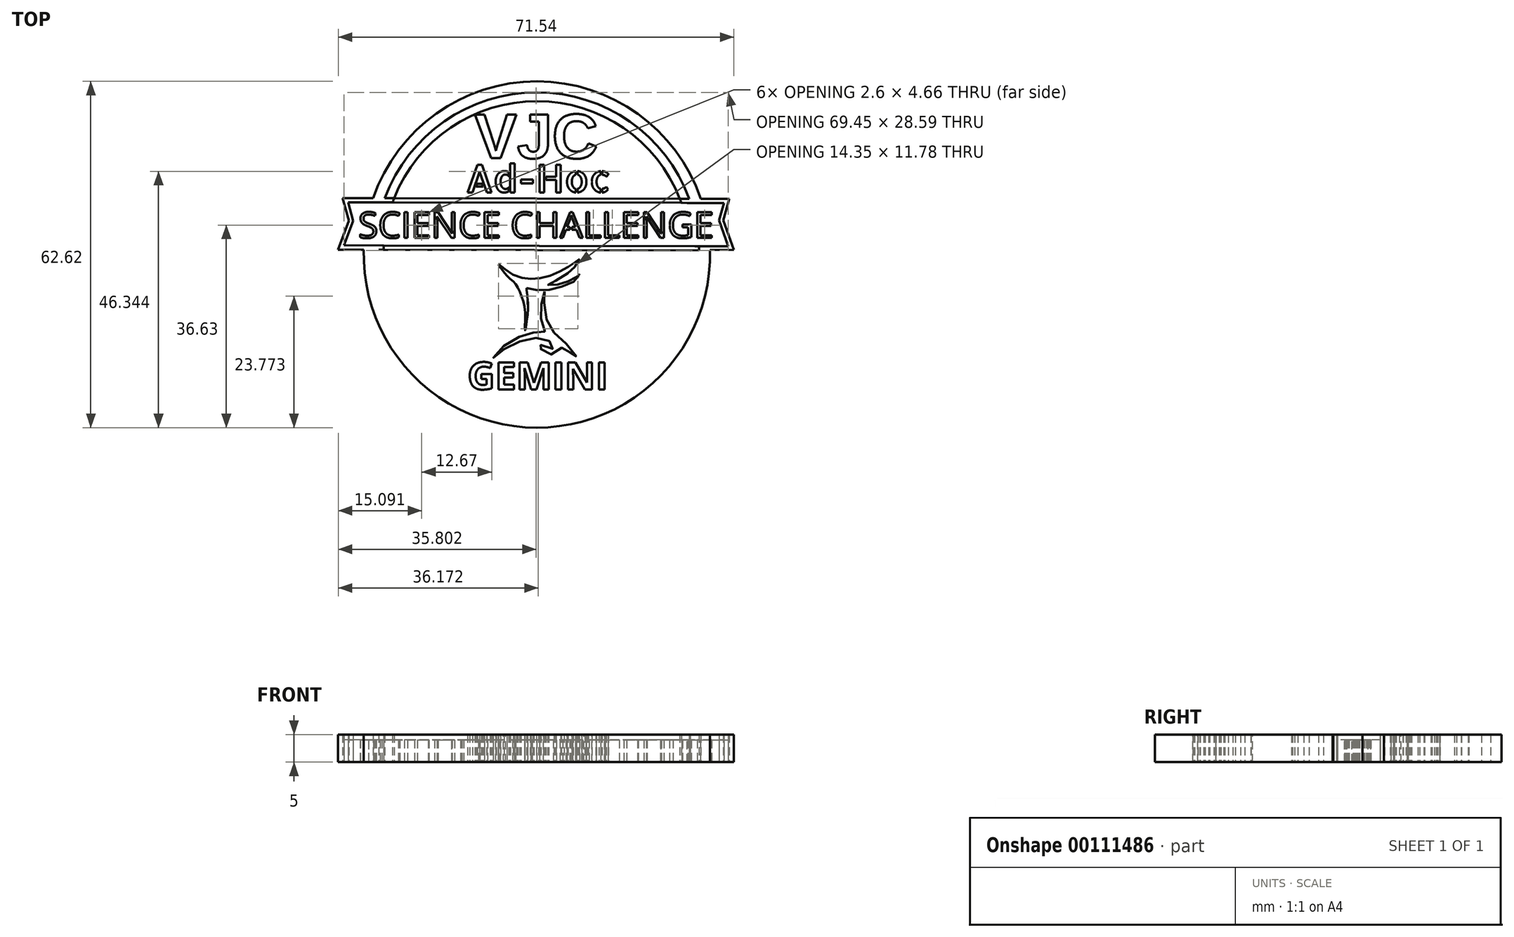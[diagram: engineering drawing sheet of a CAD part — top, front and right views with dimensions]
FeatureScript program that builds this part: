
annotation { "Feature Type Name" : "Feature", "Feature Type Description" : "" }
export const myFeature = defineFeature(function(context is Context, id is Id, definition is map)
    precondition{}
    {
        {
            var Q0;
            Q0=qCreatedBy(makeId("Top.planeOp"),FACE);
            var sketch = newSketch(context, id + "F0", { "sketchPlane" : qUnion([Q0])});
            skCircle(sketch, "E0", {"center": v(0.94, -3) * mm, "radius": 27.74 * mm});
            skPoint(sketch, "E0.first.point", {"position": v(1.58, 24.74) * mm});
            skPoint(sketch, "E0.second.point", {"position": v(0.52, -30.73) * mm});
            skPoint(sketch, "E0.third.point", {"position": v(-26.76, -1.33) * mm});
            skLineSegment(sketch, "E1", {"start": v(-24.87, 7.2) * mm, "end": v(-34.2, 7.2) * mm});
            skLineSegment(sketch, "E2", {"start": v(-34.2, 7.2) * mm, "end": v(-33.08, 3.11) * mm});
            skLineSegment(sketch, "E3", {"start": v(-33.08, 3.11) * mm, "end": v(-35, -2.1) * mm});
            skLineSegment(sketch, "E4", {"start": v(-35, -2.1) * mm, "end": v(-26.8, -2.1) * mm});
            skLineSegment(sketch, "E5", {"start": v(26.78, 7.1) * mm, "end": v(35.71, 7.1) * mm});
            skLineSegment(sketch, "E6", {"start": v(35.71, 7.1) * mm, "end": v(34.66, 3.21) * mm});
            skLineSegment(sketch, "E7", {"start": v(34.66, 3.21) * mm, "end": v(36.55, -2.1) * mm});
            skLineSegment(sketch, "E8", {"start": v(36.55, -2.1) * mm, "end": v(28.67, -2.25) * mm});
            skFitSpline(sketch, "E9", {"points": [v(-6, -4.72) * mm, v(-5.23, -5.35) * mm, v(-3.9, -6.35) * mm, v(-2.48, -6.98) * mm, v(-0.85, -7.35) * mm, v(0.35, -7.37) * mm, v(2.08, -7.15) * mm, v(3.86, -6.6) * mm, v(5.5, -5.84) * mm, v(6.83, -5.05) * mm, v(7.95, -4.34) * mm, v(8.2, -4.17) * mm, v(8.54, -3.89) * mm, v(8.14, -4.78) * mm, v(7.2, -5.82) * mm, v(5.2, -7.28) * mm, v(2.9, -8.45) * mm, v(3.98, -8.47) * mm, v(5.87, -8.12) * mm, v(7.76, -7.26) * mm, v(8.43, -6.75) * mm, v(8.6, -6.46) * mm, v(8.47, -7.15) * mm, v(6.46, -8.4) * mm, v(3.8, -9.28) * mm, v(1.11, -9.42) * mm, v(-0.95, -9.06) * mm], "startDerivative": vector(22.31, -18.25) * mm, "endDerivative": vector(-43, 9.84) * mm});
            skFitSpline(sketch, "E10", {"points": [v(-6, -4.72) * mm, v(-5.19, -6.01) * mm, v(-3.81, -7.48) * mm, v(-3.02, -8.2) * mm, v(-2.26, -9.47) * mm, v(-1.53, -11.45) * mm, v(-1.17, -13.95) * mm, v(-1.2, -16.67) * mm, v(-0.95, -15.45) * mm, v(-0.68, -11.98) * mm, v(-0.91, -9.36) * mm, v(-0.95, -9.06) * mm], "startDerivative": vector(8.3, -15) * mm, "endDerivative": vector(-0.86, 6) * mm});
            skFitSpline(sketch, "E11", {"points": [v(2.34, -9.66) * mm, v(2.02, -10.62) * mm, v(1.67, -12.76) * mm, v(1.67, -14.3) * mm, v(2.06, -16.19) * mm, v(2.36, -16.95) * mm, v(1.82, -16.92) * mm, v(-0.01, -17.17) * mm, v(-1.66, -17.64) * mm, v(-3.97, -18.79) * mm, v(-6.02, -20.44) * mm, v(-6.96, -21.68) * mm, v(-5.91, -20.77) * mm, v(-3.67, -19.33) * mm, v(-1.3, -18.4) * mm, v(0.83, -18.07) * mm, v(2.42, -18.3) * mm, v(3.7, -19.03) * mm, v(4.04, -19.68) * mm, v(3.45, -20.21) * mm, v(1.98, -19.81) * mm, v(1.3, -18.87) * mm, v(1.45, -19.8) * mm, v(2.36, -20.56) * mm, v(3.3, -21.02) * mm, v(4.84, -20.7) * mm, v(5.53, -19.8) * mm, v(6.38, -20.28) * mm, v(7.16, -20.84) * mm, v(8.14, -21.87) * mm, v(7.64, -20.68) * mm, v(6.28, -19.14) * mm, v(4.5, -17.53) * mm, v(3.33, -16.29) * mm, v(2.56, -14.18) * mm, v(2.24, -11.68) * mm, v(2.33, -10.24) * mm, v(2.34, -9.66) * mm]});
            skLineSegment(sketch, "E12", {"start": v(-24.87, 7.2) * mm, "end": v(28.1, 7.1) * mm});
            skLineSegment(sketch, "E13", {"start": v(-27.68, -2.1) * mm, "end": v(29.48, -2.24) * mm});
            skCircle(sketch, "E14.0", {"center": v(0.94, -3) * mm, "radius": 29.33 * mm});
            skCircle(sketch, "E15.0", {"center": v(0.94, -3) * mm, "radius": 31.31 * mm});
            skLineSegment(sketch, "E16.0", {"start": v(-24.87, 6.45) * mm, "end": v(28.1, 6.35) * mm});
            skLineSegment(sketch, "E17.0", {"start": v(-24.87, 6.45) * mm, "end": v(-33.21, 6.45) * mm});
            skLineSegment(sketch, "E18", {"start": v(28.1, 6.35) * mm, "end": v(34.73, 6.35) * mm});
            skLineSegment(sketch, "E19.0", {"start": v(-27.68, -1.35) * mm, "end": v(29.48, -1.49) * mm});
            skLineSegment(sketch, "E20", {"start": v(-27.68, -1.35) * mm, "end": v(-33.91, -1.33) * mm});
            skLineSegment(sketch, "E21", {"start": v(29.48, -1.49) * mm, "end": v(35.54, -1.5) * mm});
            skLineSegment(sketch, "E22.0", {"start": v(34.73, 6.35) * mm, "end": v(33.88, 3.18) * mm});
            skLineSegment(sketch, "E23.0", {"start": v(33.88, 3.18) * mm, "end": v(35.54, -1.5) * mm});
            skLineSegment(sketch, "E24.0", {"start": v(-32.3, 3.08) * mm, "end": v(-33.91, -1.33) * mm});
            skLineSegment(sketch, "E25.trimOffspring", {"start": v(-33.21, 6.45) * mm, "end": v(-32.3, 3.08) * mm});
            skText(sketch, "E26", { "text": "SCIENCE CHALLENGE", "fontName": "OpenSans-Regular.ttf"});
            skText(sketch, "E27", { "text": "GEMINI", "fontName": "OpenSans-Bold.ttf"});
            skText(sketch, "E28", { "text": "VJC", "fontName": "Arimo-Bold.ttf"});
            skLineSegment(sketch, "E29", {"start": v(6.9, 1.33) * mm, "end": v(6.9, 2.22) * mm});
            skLineSegment(sketch, "E30", {"start": v(6.9, 2.22) * mm, "end": v(7.18, 2.22) * mm});
            skLineSegment(sketch, "E31", {"start": v(7.18, 2.22) * mm, "end": v(7.26, 2.22) * mm});
            skLineSegment(sketch, "E32", {"start": v(7.26, 2.22) * mm, "end": v(7.26, 1.34) * mm});
            skLineSegment(sketch, "E33", {"start": v(7.26, 1.34) * mm, "end": v(6.9, 1.33) * mm});
            skText(sketch, "E34", { "text": "Ad-Hoc", "fontName": "AllertaStencil-Regular.ttf"});
            const initialGuessF0  = {"E26": [-0.03136, 0, 1, 0, 0.0047], "E27": [-0.0116, -0.02738, 1, 0, 0.00494], "E28": [-0.01032, 0.01442, 1, 0, 0.00826], "E34": [-0.012, 0.00825, 1, 0, 0.005]};
            skSetInitialGuess(sketch, initialGuessF0);
            skSolve(sketch);
        }
        {
            var Q0;
            Q0=makeQuery(id+"F0.imprint","IMPRINT",FACE,{"disambiguationData":[TD([[makeQuery(id+"F0.imprint","IMPRINT",EDGE,{"derivedFrom":sQuery(id+"F0.wireOp",EDGE,"f2c7ee9f-897c-4c1d-89b3-a48ac7c6bfa7.sketch_text.stroke-0")}),1.0]])]});
            var Q1;
            {var subQ0=sQuery(id+"F0.wireOp",EDGE,"E15.0");var subQ1=sQuery(id+"F0.wireOp",EDGE,"E1");var subQ2=makeQuery(id+"F0.imprint","INTERSECT",VERTEX,{"derivedFrom":[subQ1,subQ0]});Q1=makeQuery(id+"F0.imprint","IMPRINT",FACE,{"disambiguationData":[TD([[makeQuery(id+"F0.imprint","IMPRINT",EDGE,{"disambiguationData":[TD([[subQ2,1.0]])],"derivedFrom":subQ1}),-1.0]])]});}
            var Q2;
            Q2=makeQuery(id+"F0.imprint","IMPRINT",FACE,{"disambiguationData":[TD([[makeQuery(id+"F0.imprint","IMPRINT",EDGE,{"derivedFrom":sQuery(id+"F0.wireOp",EDGE,"26462852-2f77-49b2-9a3d-6dfd93b606f1.sketch_text.stroke-0")}),1.0]])]});
            var Q3;
            {var subQ0=sQuery(id+"F0.wireOp",EDGE,"E15.0");var subQ1=sQuery(id+"F0.wireOp",EDGE,"E4");var subQ2=makeQuery(id+"F0.imprint","INTERSECT",VERTEX,{"derivedFrom":[subQ1,subQ0]});Q3=makeQuery(id+"F0.imprint","IMPRINT",FACE,{"disambiguationData":[TD([[makeQuery(id+"F0.imprint","IMPRINT",EDGE,{"disambiguationData":[TD([[subQ2,-1.0]])],"derivedFrom":subQ1}),-1.0]])]});}
            var Q4;
            {var subQ7=sQuery(id+"F0.wireOp",EDGE,"E2");Q4=makeQuery(id+"F0.imprint","IMPRINT",FACE,{"disambiguationData":[TD([[makeQuery(id+"F0.imprint","IMPRINT",EDGE,{"derivedFrom":subQ7}),1.0]])]});}
            var Q5;
            {var subQ3=sQuery(id+"F0.wireOp",EDGE,"E17.0");var subQ10=makeQuery(id+"F0.imprint","IMPRINT",VERTEX,{"derivedFrom":subQ3});Q5=makeQuery(id+"F0.imprint","IMPRINT",FACE,{"disambiguationData":[TD([[makeQuery(id+"F0.imprint","IMPRINT",EDGE,{"disambiguationData":[TD([[subQ10,1.0]])],"derivedFrom":subQ3}),-1.0]])]});}
            var Q6;
            {var subQ0=sQuery(id+"F0.wireOp",EDGE,"E1");var subQ5=sQuery(id+"F0.wireOp",EDGE,"E14.0");var subQ6=makeQuery(id+"F0.imprint","INTERSECT",VERTEX,{"derivedFrom":[subQ0,subQ5]});Q6=makeQuery(id+"F0.imprint","IMPRINT",FACE,{"disambiguationData":[TD([[makeQuery(id+"F0.imprint","IMPRINT",EDGE,{"disambiguationData":[TD([[subQ6,-1.0]])],"derivedFrom":subQ5}),1.0]])]});}
            var Q7;
            {var subQ1=sQuery(id+"F0.wireOp",EDGE,"E5");var subQ6=sQuery(id+"F0.wireOp",EDGE,"E0");var subQ7=makeQuery(id+"F0.imprint","INTERSECT",VERTEX,{"derivedFrom":[subQ6,subQ1]});Q7=makeQuery(id+"F0.imprint","IMPRINT",FACE,{"disambiguationData":[TD([[makeQuery(id+"F0.imprint","IMPRINT",EDGE,{"disambiguationData":[TD([[subQ7,1.0]])],"derivedFrom":subQ6}),-1.0]])]});}
            var Q8;
            {var subQ0=sQuery(id+"F0.wireOp",EDGE,"E15.0");var subQ1=sQuery(id+"F0.wireOp",EDGE,"E5");var subQ2=makeQuery(id+"F0.imprint","INTERSECT",VERTEX,{"derivedFrom":[subQ1,subQ0]});Q8=makeQuery(id+"F0.imprint","IMPRINT",FACE,{"disambiguationData":[TD([[makeQuery(id+"F0.imprint","IMPRINT",EDGE,{"disambiguationData":[TD([[subQ2,1.0]])],"derivedFrom":subQ1}),-1.0]])]});}
            var Q9;
            {var subQ11=sQuery(id+"F0.wireOp",EDGE,"E6");Q9=makeQuery(id+"F0.imprint","IMPRINT",FACE,{"disambiguationData":[TD([[makeQuery(id+"F0.imprint","IMPRINT",EDGE,{"derivedFrom":subQ11}),-1.0]])]});}
            var Q10;
            {var subQ0=sQuery(id+"F0.wireOp",EDGE,"E13");var subQ1=sQuery(id+"F0.wireOp",EDGE,"E0");var subQ2=makeQuery(id+"F0.imprint","INTERSECT",VERTEX,{"disambiguationData":[OD(0.0)],"derivedFrom":[subQ1,subQ0]});Q10=makeQuery(id+"F0.imprint","IMPRINT",FACE,{"disambiguationData":[TD([[makeQuery(id+"F0.imprint","IMPRINT",EDGE,{"disambiguationData":[TD([[subQ2,-1.0]])],"derivedFrom":subQ1}),1.0]])]});}
            var Q11;
            {var subQ0=sQuery(id+"F0.wireOp",EDGE,"E13");var subQ3=sQuery(id+"F0.wireOp",EDGE,"E0");var subQ4=makeQuery(id+"F0.imprint","INTERSECT",VERTEX,{"disambiguationData":[OD(0.0)],"derivedFrom":[subQ3,subQ0]});Q11=makeQuery(id+"F0.imprint","IMPRINT",FACE,{"disambiguationData":[TD([[makeQuery(id+"F0.imprint","IMPRINT",EDGE,{"disambiguationData":[TD([[subQ4,-1.0]])],"derivedFrom":subQ3}),-1.0]])]});}
            var Q12;
            {var subQ0=sQuery(id+"F0.wireOp",EDGE,"E15.0");var subQ1=sQuery(id+"F0.wireOp",EDGE,"E8");var subQ2=makeQuery(id+"F0.imprint","INTERSECT",VERTEX,{"derivedFrom":[subQ1,subQ0]});Q12=makeQuery(id+"F0.imprint","IMPRINT",FACE,{"disambiguationData":[TD([[makeQuery(id+"F0.imprint","IMPRINT",EDGE,{"disambiguationData":[TD([[subQ2,-1.0]])],"derivedFrom":subQ1}),-1.0]])]});}
            var Q13;
            {var subQ0=sQuery(id+"F0.wireOp",EDGE,"E15.0");var subQ1=sQuery(id+"F0.wireOp",EDGE,"E1");var subQ2=makeQuery(id+"F0.imprint","INTERSECT",VERTEX,{"derivedFrom":[subQ1,subQ0]});Q13=makeQuery(id+"F0.imprint","IMPRINT",FACE,{"disambiguationData":[TD([[makeQuery(id+"F0.imprint","IMPRINT",EDGE,{"disambiguationData":[TD([[subQ2,1.0]])],"derivedFrom":subQ1}),1.0]])]});}
            var Q14;
            {var subQ0=sQuery(id+"F0.wireOp",EDGE,"E15.0");var subQ1=sQuery(id+"F0.wireOp",EDGE,"E4");var subQ2=makeQuery(id+"F0.imprint","INTERSECT",VERTEX,{"derivedFrom":[subQ1,subQ0]});Q14=makeQuery(id+"F0.imprint","IMPRINT",FACE,{"disambiguationData":[TD([[makeQuery(id+"F0.imprint","IMPRINT",EDGE,{"disambiguationData":[TD([[subQ2,-1.0]])],"derivedFrom":subQ1}),1.0]])]});}
            var Q15;
            {var subQ0=sQuery(id+"F0.wireOp",EDGE,"E4");var subQ1=sQuery(id+"F0.wireOp",EDGE,"E0");var subQ2=makeQuery(id+"F0.imprint","INTERSECT",VERTEX,{"derivedFrom":[subQ1,subQ0]});Q15=makeQuery(id+"F0.imprint","IMPRINT",FACE,{"disambiguationData":[TD([[makeQuery(id+"F0.imprint","IMPRINT",EDGE,{"disambiguationData":[TD([[subQ2,1.0]])],"derivedFrom":subQ1}),-1.0]])]});}
            var Q16;
            Q16=makeQuery(id+"F0.imprint","IMPRINT",FACE,{"disambiguationData":[TD([[makeQuery(id+"F0.imprint","IMPRINT",EDGE,{"derivedFrom":sQuery(id+"F0.wireOp",EDGE,"E9")}),1.0]])]});
            var Q17;
            Q17=makeQuery(id+"F0.imprint","IMPRINT",FACE,{"disambiguationData":[TD([[makeQuery(id+"F0.imprint","IMPRINT",EDGE,{"derivedFrom":sQuery(id+"F0.wireOp",EDGE,"E28.sketch_text.stroke-0")}),1.0]])]});
            extrude(context, id + "F1", {"entities" : qUnion([Q0, Q1, Q2, Q3, Q4, Q5, Q6, Q7, Q8, Q9, Q10, Q11, Q12, Q13, Q14, Q15, Q16, Q17]), "depth" : 5 * mm});
        }
        {
            var Q0;
            {var subQ0=sQuery(id+"F0.wireOp",EDGE,"E24.0");Q0=makeQuery(id+"F0.imprint","IMPRINT",FACE,{"disambiguationData":[TD([[makeQuery(id+"F0.imprint","IMPRINT",EDGE,{"derivedFrom":subQ0}),1.0]])]});}
            var Q1;
            {var subQ11=sQuery(id+"F0.wireOp",EDGE,"E26.sketch_text.stroke-16");Q1=makeQuery(id+"F0.imprint","IMPRINT",FACE,{"disambiguationData":[TD([[makeQuery(id+"F0.imprint","IMPRINT",EDGE,{"derivedFrom":subQ11}),1.0]])]});}
            var Q2;
            {var subQ0=sQuery(id+"F0.wireOp",EDGE,"E26.sketch_text.stroke-33");Q2=makeQuery(id+"F0.imprint","IMPRINT",FACE,{"disambiguationData":[TD([[makeQuery(id+"F0.imprint","IMPRINT",EDGE,{"derivedFrom":subQ0}),1.0]])]});}
            var Q3;
            {var subQ10=sQuery(id+"F0.wireOp",EDGE,"E26.sketch_text.stroke-28");Q3=makeQuery(id+"F0.imprint","IMPRINT",FACE,{"disambiguationData":[TD([[makeQuery(id+"F0.imprint","IMPRINT",EDGE,{"derivedFrom":subQ10}),1.0]])]});}
            var Q4;
            {var subQ25=sQuery(id+"F0.wireOp",EDGE,"E26.sketch_text.stroke-178");Q4=makeQuery(id+"F0.imprint","IMPRINT",FACE,{"disambiguationData":[TD([[makeQuery(id+"F0.imprint","IMPRINT",EDGE,{"derivedFrom":subQ25}),1.0]])]});}
            var Q5;
            {var subQ1=sQuery(id+"F0.wireOp",EDGE,"E26.sketch_text.stroke-198");var subQ3=sQuery(id+"F0.wireOp",EDGE,"E14.0");var subQ4=makeQuery(id+"F0.imprint","INTERSECT",VERTEX,{"derivedFrom":[subQ3,subQ1]});Q5=makeQuery(id+"F0.imprint","IMPRINT",FACE,{"disambiguationData":[TD([[makeQuery(id+"F0.imprint","IMPRINT",EDGE,{"disambiguationData":[TD([[subQ4,-1.0]])],"derivedFrom":subQ3}),-1.0]])]});}
            var Q6;
            {var subQ8=sQuery(id+"F0.wireOp",EDGE,"E22.0");Q6=makeQuery(id+"F0.imprint","IMPRINT",FACE,{"disambiguationData":[TD([[makeQuery(id+"F0.imprint","IMPRINT",EDGE,{"derivedFrom":subQ8}),-1.0]])]});}
            var Q7;
            {var subQ0=sQuery(id+"F0.wireOp",EDGE,"E26.sketch_text.stroke-6");Q7=makeQuery(id+"F0.imprint","IMPRINT",FACE,{"disambiguationData":[TD([[makeQuery(id+"F0.imprint","IMPRINT",EDGE,{"derivedFrom":subQ0}),1.0]])]});}
            var Q8;
            {var subQ6=sQuery(id+"F0.wireOp",EDGE,"E26.sketch_text.stroke-1");Q8=makeQuery(id+"F0.imprint","IMPRINT",FACE,{"disambiguationData":[TD([[makeQuery(id+"F0.imprint","IMPRINT",EDGE,{"derivedFrom":subQ6}),1.0]])]});}
            var Q9;
            {var subQ6=sQuery(id+"F0.wireOp",EDGE,"E26.sketch_text.stroke-189");Q9=makeQuery(id+"F0.imprint","IMPRINT",FACE,{"disambiguationData":[TD([[makeQuery(id+"F0.imprint","IMPRINT",EDGE,{"derivedFrom":subQ6}),1.0]])]});}
            var Q10;
            {var subQ5=sQuery(id+"F0.wireOp",EDGE,"E26.sketch_text.stroke-202");Q10=makeQuery(id+"F0.imprint","IMPRINT",FACE,{"disambiguationData":[TD([[makeQuery(id+"F0.imprint","IMPRINT",EDGE,{"derivedFrom":subQ5}),1.0]])]});}
            var Q11;
            {var subQ5=sQuery(id+"F0.wireOp",EDGE,"E26.sketch_text.stroke-206");Q11=makeQuery(id+"F0.imprint","IMPRINT",FACE,{"disambiguationData":[TD([[makeQuery(id+"F0.imprint","IMPRINT",EDGE,{"derivedFrom":subQ5}),1.0]])]});}
            var Q12;
            {var subQ0=sQuery(id+"F0.wireOp",EDGE,"E21");var subQ1=sQuery(id+"F0.wireOp",EDGE,"E14.0");var subQ2=makeQuery(id+"F0.imprint","INTERSECT",VERTEX,{"derivedFrom":[subQ1,subQ0]});Q12=makeQuery(id+"F0.imprint","IMPRINT",FACE,{"disambiguationData":[TD([[makeQuery(id+"F0.imprint","IMPRINT",EDGE,{"disambiguationData":[TD([[subQ2,-1.0]])],"derivedFrom":subQ1}),-1.0]])]});}
            var Q13;
            Q13=makeQuery(id+"F0.imprint","IMPRINT",FACE,{"disambiguationData":[TD([[makeQuery(id+"F0.imprint","IMPRINT",EDGE,{"derivedFrom":sQuery(id+"F0.wireOp",EDGE,"E26.sketch_text.stroke-133")}),1.0]])]});
            var Q14;
            {var subQ5=sQuery(id+"F0.wireOp",EDGE,"E26.sketch_text.stroke-26");Q14=makeQuery(id+"F0.imprint","IMPRINT",FACE,{"disambiguationData":[TD([[makeQuery(id+"F0.imprint","IMPRINT",EDGE,{"derivedFrom":subQ5}),1.0]])]});}
            var Q15;
            {var subQ1=sQuery(id+"F0.wireOp",EDGE,"E26.sketch_text.stroke-19");Q15=makeQuery(id+"F0.imprint","IMPRINT",FACE,{"disambiguationData":[TD([[makeQuery(id+"F0.imprint","IMPRINT",EDGE,{"derivedFrom":subQ1}),1.0]])]});}
            var Q16;
            {var subQ5=sQuery(id+"F0.wireOp",EDGE,"E33");Q16=makeQuery(id+"F0.imprint","IMPRINT",FACE,{"disambiguationData":[TD([[makeQuery(id+"F0.imprint","IMPRINT",EDGE,{"derivedFrom":subQ5}),-1.0]])]});}
            var Q17;
            {var subQ0=sQuery(id+"F0.wireOp",EDGE,"E32");var subQ1=sQuery(id+"F0.wireOp",EDGE,"E26.sketch_text.stroke-126");var subQ2=makeQuery(id+"F0.imprint","INTERSECT",VERTEX,{"derivedFrom":[subQ1,subQ0]});Q17=makeQuery(id+"F0.imprint","IMPRINT",FACE,{"disambiguationData":[TD([[makeQuery(id+"F0.imprint","IMPRINT",EDGE,{"disambiguationData":[TD([[subQ2,-1.0]])],"derivedFrom":subQ1}),-1.0]])]});}
            var Q18;
            {var subQ1=sQuery(id+"F0.wireOp",EDGE,"E30");Q18=makeQuery(id+"F0.imprint","IMPRINT",FACE,{"disambiguationData":[TD([[makeQuery(id+"F0.imprint","IMPRINT",EDGE,{"derivedFrom":subQ1}),-1.0]])]});}
            extrude(context, id + "F2", {"entities" : qUnion([Q0, Q1, Q2, Q3, Q4, Q5, Q6, Q7, Q8, Q9, Q10, Q11, Q12, Q13, Q14, Q15, Q16, Q17, Q18]), "depth" : 4 * mm});
        }
    });
